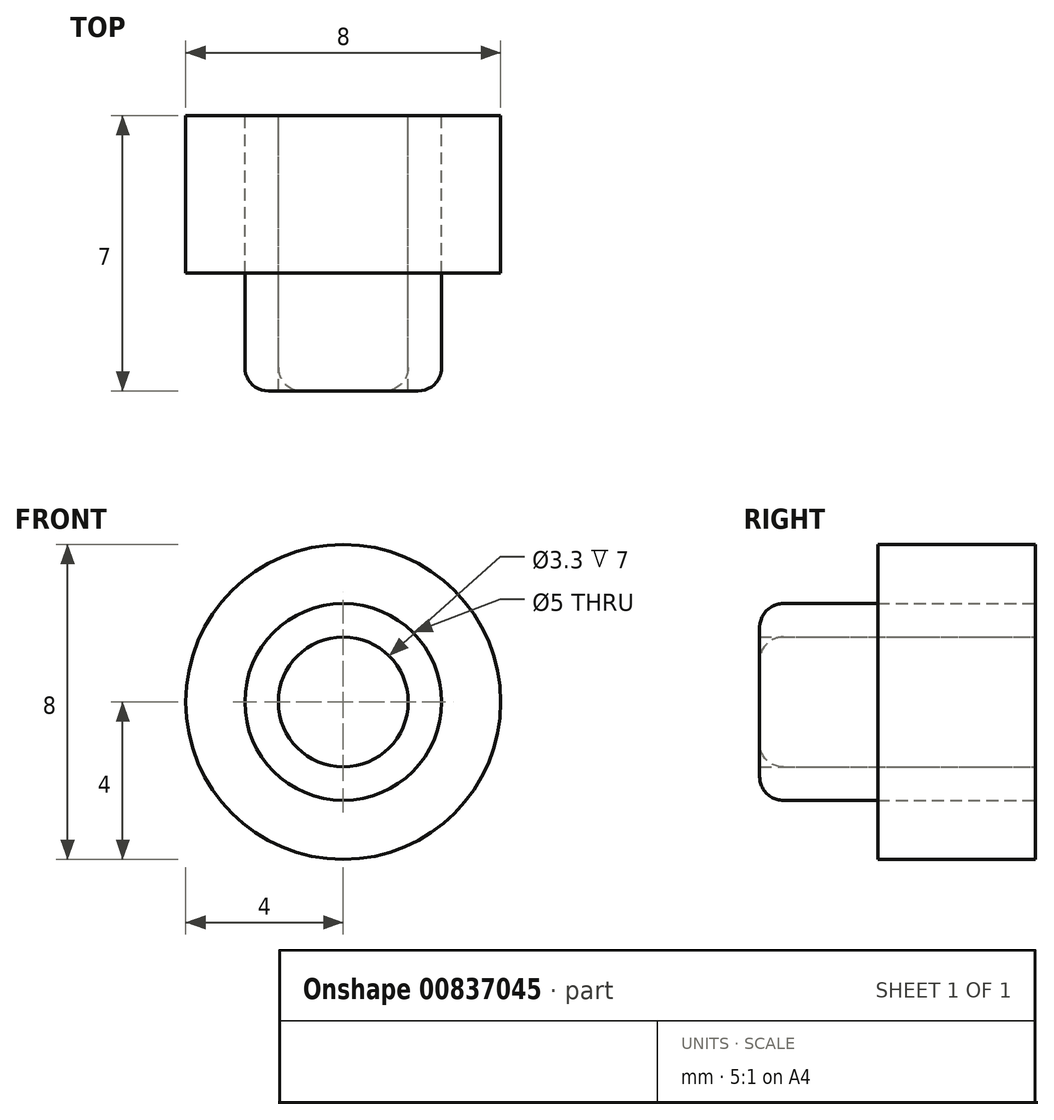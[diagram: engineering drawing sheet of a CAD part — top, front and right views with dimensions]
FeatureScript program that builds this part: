
annotation { "Feature Type Name" : "Feature", "Feature Type Description" : "" }
export const myFeature = defineFeature(function(context is Context, id is Id, definition is map)
    precondition{}
    {
        {
            var Q0;
            Q0=qCreatedBy(makeId("Front.planeOp"),FACE);
            var sketch = newSketch(context, id + "F0", { "sketchPlane" : qUnion([Q0])});
            skCircle(sketch, "E0", {"center": v(0, 0) * mm, "radius": 4 * mm});
            skCircle(sketch, "E1", {"center": v(0, 0) * mm, "radius": 1.65 * mm});
            skCircle(sketch, "E2", {"center": v(0, 0) * mm, "radius": 2.5 * mm});
            skSolve(sketch);
        }
        {
            var Q0;
            Q0=makeQuery(id+"F0.imprint","IMPRINT",FACE,{"disambiguationData":[TD([[makeQuery(id+"F0.imprint","IMPRINT",EDGE,{"derivedFrom":sQuery(id+"F0.wireOp",EDGE,"E1")}),1.0]])]});
            var Q1;
            Q1=sQuery(id+"F0.wireOp",EDGE,"E1");
            extrude(context, id + "F1", {"entities" : qUnion([Q0]), "surfaceEntities" : qUnion([Q1]), "depth" : 7 * mm, "offsetDistance" : 25 * mm});
        }
        {
            var Q0;
            Q0=makeQuery(id+"F0.imprint","IMPRINT",FACE,{"disambiguationData":[TD([[makeQuery(id+"F0.imprint","IMPRINT",EDGE,{"derivedFrom":sQuery(id+"F0.wireOp",EDGE,"E1")}),-1.0]])]});
            var Q1;
            Q1=sQuery(id+"F0.wireOp",EDGE,"E2");
            extrude(context, id + "F2", {"entities" : qUnion([Q0]), "surfaceEntities" : qUnion([Q1]), "depth" : 7 * mm, "offsetDistance" : 25 * mm});
        }
        {
            var Q0;
            Q0=makeQuery(id+"F0.imprint","IMPRINT",FACE,{"disambiguationData":[TD([[makeQuery(id+"F0.imprint","IMPRINT",EDGE,{"derivedFrom":sQuery(id+"F0.wireOp",EDGE,"E0")}),1.0]])]});
            extrude(context, id + "F3", {"entities" : qUnion([Q0]), "depth" : 4 * mm, "offsetDistance" : 25 * mm});
        }
        {
            var Q0;
            Q0=makeQuery(id+"F1.opExtrude","CAP_EDGE",EDGE,{"disambiguationData":[OSD([sQuery(id+"F0.wireOp",EDGE,"E1")])],"isStart":false});
            var Q1;
            Q1=makeQuery(id+"F2.opExtrude","CAP_EDGE",EDGE,{"disambiguationData":[OSD([sQuery(id+"F0.wireOp",EDGE,"E2")])],"isStart":false});
            fillet(context, id + "F4", {"entities" : qUnion([Q0, Q1]), "radius" : 0.6 * mm, "tangentPropagation" : true, "allowEdgeOverflow" : false});
        }
    });
